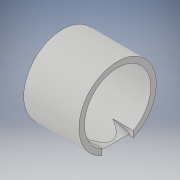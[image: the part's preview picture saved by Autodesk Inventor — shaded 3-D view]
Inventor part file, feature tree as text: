
AUTODESK INVENTOR PART (.ipt)
format: ipt  version: 2019 (Build 230136000, 136)  size: 126,976 bytes
history: native  units: in
note: dims shown in document units (in); Inventor stores cm internally (conversion verified against a paired STEP export)
features: sketch x2, plane x1, revolve x1, extrude x1
ambient origin geometry x8: Origin, YZ Plane, XZ Plane, XY Plane, X Axis, Y Axis, Z Axis, Center Point
bodies: Solid1 (feature_tree)
feature tree (5):
  plane  "Work Plane1"
  revolve  "Revolution1"  [1 undecoded]
  extrude  "Extrusion2"  Depth=0.6693in
  sketch  "Sketch2"  dims[d11=1.1811in d12=0.1181in]
  sketch  "Sketch3"  dims[d15=90.0deg d17=0.6693in d19=15.0deg d20=15.0deg d21=0.1063in d23=1.1024in d24=0.2047in d25=0.2091in d26=0.2726in d27=0.6693in d28=0.0in d29=1.6535in]
note: 1 required parameter value undecoded (feature->parameter linkage not recoverable at this tier; creation-order binding heuristic only, values carry confidence <= 0.55)
